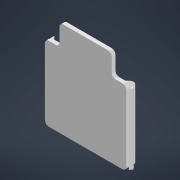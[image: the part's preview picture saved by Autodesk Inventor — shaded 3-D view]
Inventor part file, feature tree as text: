
AUTODESK INVENTOR PART (.ipt)
format: ipt  version: 2022 (Build 260153000, 153)  size: 350,720 bytes
history: native  units: in
note: dims shown in document units (in); Inventor stores cm internally (conversion verified against a paired STEP export)
features: reference x17, extrude x9, sketch x8, projected_geometry x6, other x3, plane x1, chamfer x1, shell x1
ambient origin geometry x8: Origin, YZ Plane, XZ Plane, XY Plane, X Axis, Y Axis, Z Axis, Center Point
bodies: Solid1 (feature_tree)
feature tree (46):
  extrude  "Extrusion1"  Depth=0.2362in TaperAngle=0.0deg
  sketch  "Sketch3"  dims[d3=0.2323in d4=0.0in d5=0.0039in]
  plane  "Work Plane1"
  other  "Work Point1"
  extrude  "Extrusion2"  Depth=0.0039in
  extrude  "Extrusion3"  Depth=0.1378in
  extrude  "Extrusion4"  Depth=0.1181in
  extrude  "Extrusion8"  Depth=0.002in
  extrude  "Extrusion5"  Depth=0.3937in
  chamfer  "Chamfer1"  Distance=0.0197in
  extrude  "Extrusion6"  Depth=0.0394in
  extrude  "Extrusion7"  Depth=0.0394in
  extrude  "Extrusion9"  Depth=0.0591in TaperAngle=0.0deg
  sketch  "Sketch2"  dims[d0=0.0039in d1=0.2362in d2=0.0in]
  reference  "Reference10"
  reference  "Reference11"
  reference  "Reference14"
  sketch  "Sketch4"  dims[d7=0.0039in d8=0.1378in]
  reference  "Reference15"
  projected_geometry  "Projected Loop1"
  projected_geometry  "Projected Loop2"
  projected_geometry  "Projected Loop3"
  reference  "Reference16"
  projected_geometry  "Projected Loop4"
  sketch  "Sketch6"  dims[d9=0.1181in d10=0.1181in]
  reference  "Reference17"
  reference  "Reference18"
  reference  "Reference19"
  reference  "Reference20"
  sketch  "Sketch7"  dims[d11=0.0in d12=0.0in d13=0.002in]
  reference  "Reference21"
  reference  "Reference22"
  reference  "Reference23"
  reference  "Reference24"
  sketch  "Sketch8"  dims[d14=0.2323in d15=0.0in d16=0.3937in d17=0.0197in d18=0.0in]
  sketch  "Sketch9"  dims[d19=0.0197in d20=0.0787in d21=45.0deg d22=0.0394in]
  projected_geometry  "Projected Loop5"
  projected_geometry  "Projected Loop6"
  sketch  "Sketch10"  dims[d23=0.0039in d24=0.0394in d25=0.0591in d26=0.0in d28=0.0118in d29=0.0118in d30=0.3937in d31=0.0079in d32=0.0in d33=0.0787in d34=0.7874in d35=0.5906in d36=1.9685in d38=0.1575in d39=0.3937in d41=0.3937in d43=0.1181in d45=1.0639in d46=0.0394in d47=0.0in d48=0.3937in d49=0.0in d50=0.3937in d51=0.0in]
  reference  "Reference25"
  reference  "Reference26"
  reference  "Reference27"
  reference  "Reference28"
  parser-record x1  (decoder bookkeeping rows leaked as tree rows — omitted from the tree; the rows remain in map.json)
  other  "case_assembly.iam"
  shell  "shell:1"  Thickness=0.0118in
note: 1 file-system path scrubbed to <path> (originals preserved in map.json)
